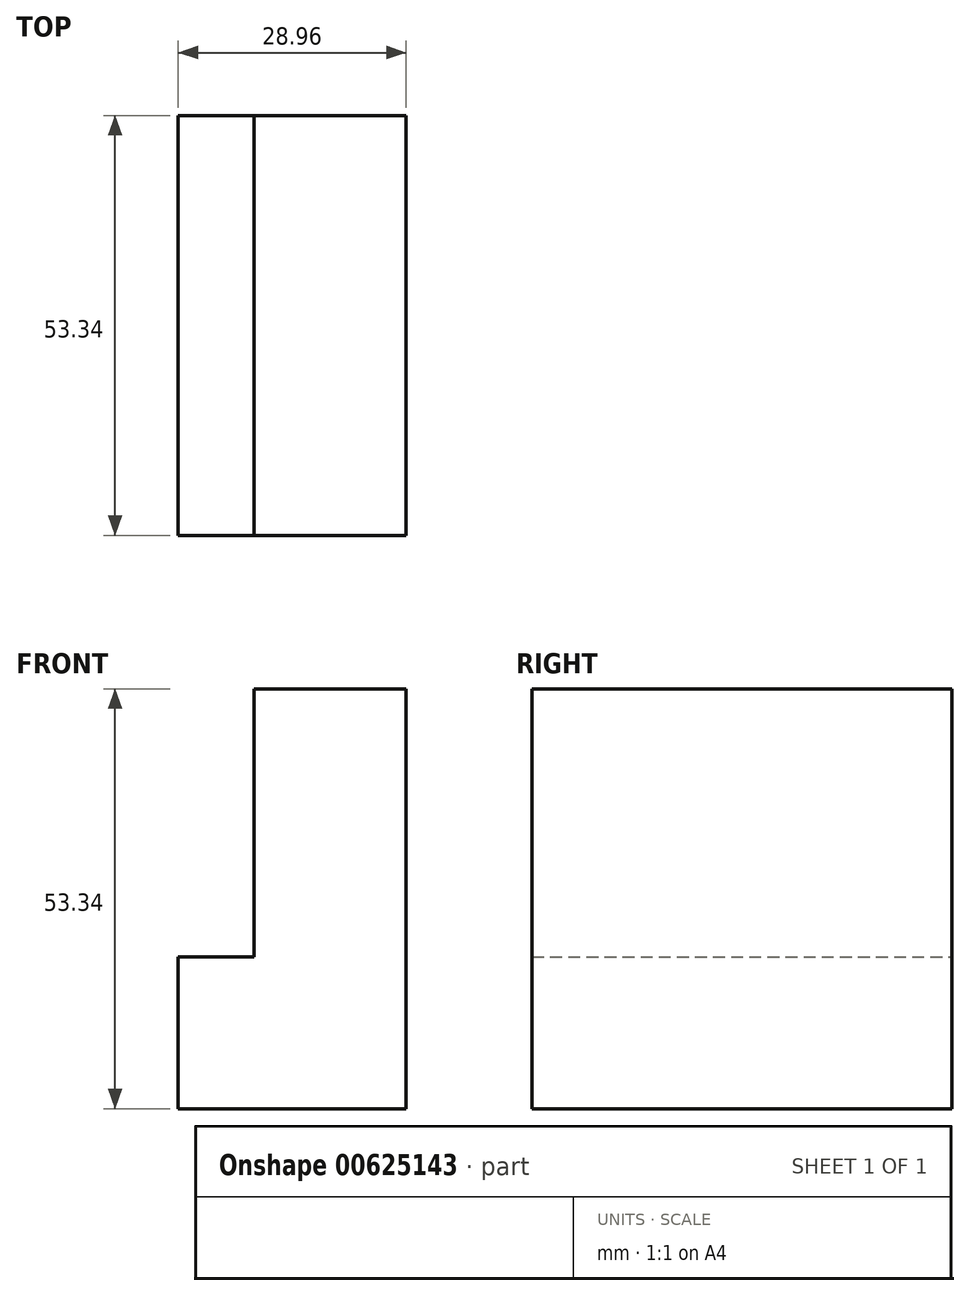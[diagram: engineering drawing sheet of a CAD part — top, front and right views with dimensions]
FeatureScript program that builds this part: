
annotation { "Feature Type Name" : "Feature", "Feature Type Description" : "" }
export const myFeature = defineFeature(function(context is Context, id is Id, definition is map)
    precondition{}
    {
        {
            var Q0;
            Q0=qCreatedBy(makeId("Front.planeOp"),FACE);
            var sketch = newSketch(context, id + "F0", { "sketchPlane" : qUnion([Q0])});
            skLineSegment(sketch, "E0", {"start": v(0, 0) * mm, "end": v(28.96, 0) * mm});
            skLineSegment(sketch, "E1", {"start": v(28.96, 0) * mm, "end": v(28.96, 53.34) * mm});
            skLineSegment(sketch, "E2", {"start": v(28.96, 53.34) * mm, "end": v(9.65, 53.34) * mm});
            skLineSegment(sketch, "E3", {"start": v(9.65, 53.34) * mm, "end": v(9.65, 19.3) * mm});
            skLineSegment(sketch, "E4", {"start": v(9.65, 19.3) * mm, "end": v(0, 19.3) * mm});
            skLineSegment(sketch, "E5", {"start": v(0, 19.3) * mm, "end": v(0, 0) * mm});
            skSolve(sketch);
        }
        {
            var Q0;
            Q0 = qSketchRegion(id + "F0", true);
            extrude(context, id + "F1", {"entities" : qUnion([Q0]), "depth" : 53.34 * mm, "offsetDistance" : 25.4 * mm});
        }
    });
